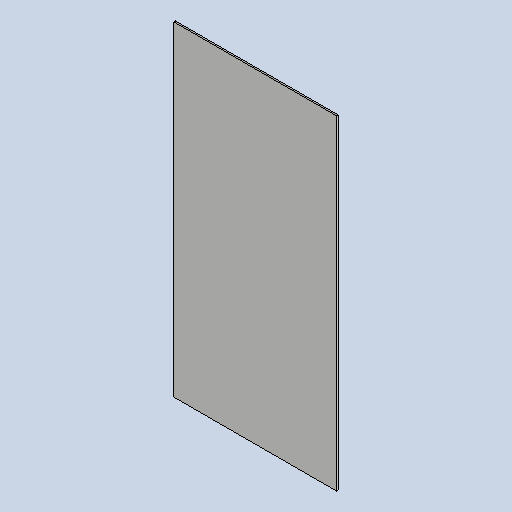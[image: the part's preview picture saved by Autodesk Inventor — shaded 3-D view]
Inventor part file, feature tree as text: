
AUTODESK INVENTOR PART (.ipt)
format: ipt  version: 2025 (Build 290162010, 162A)  size: 245,248 bytes
history: native  units: mm
features: other x2, sheet_metal_op x1, sketch x1
ambient origin geometry x8: Origin, YZ Plane, XZ Plane, XY Plane, X Axis, Y Axis, Z Axis, Center Point
bodies: Body1 (feature_tree)
feature tree (4):
  sheet_metal_op  "Face2"
  sketch  "Sketch1"  dims[d0=400.0mm d1=200.2mm d3=2.0mm]
  other  "Plate2"
  other  "Definition1"
